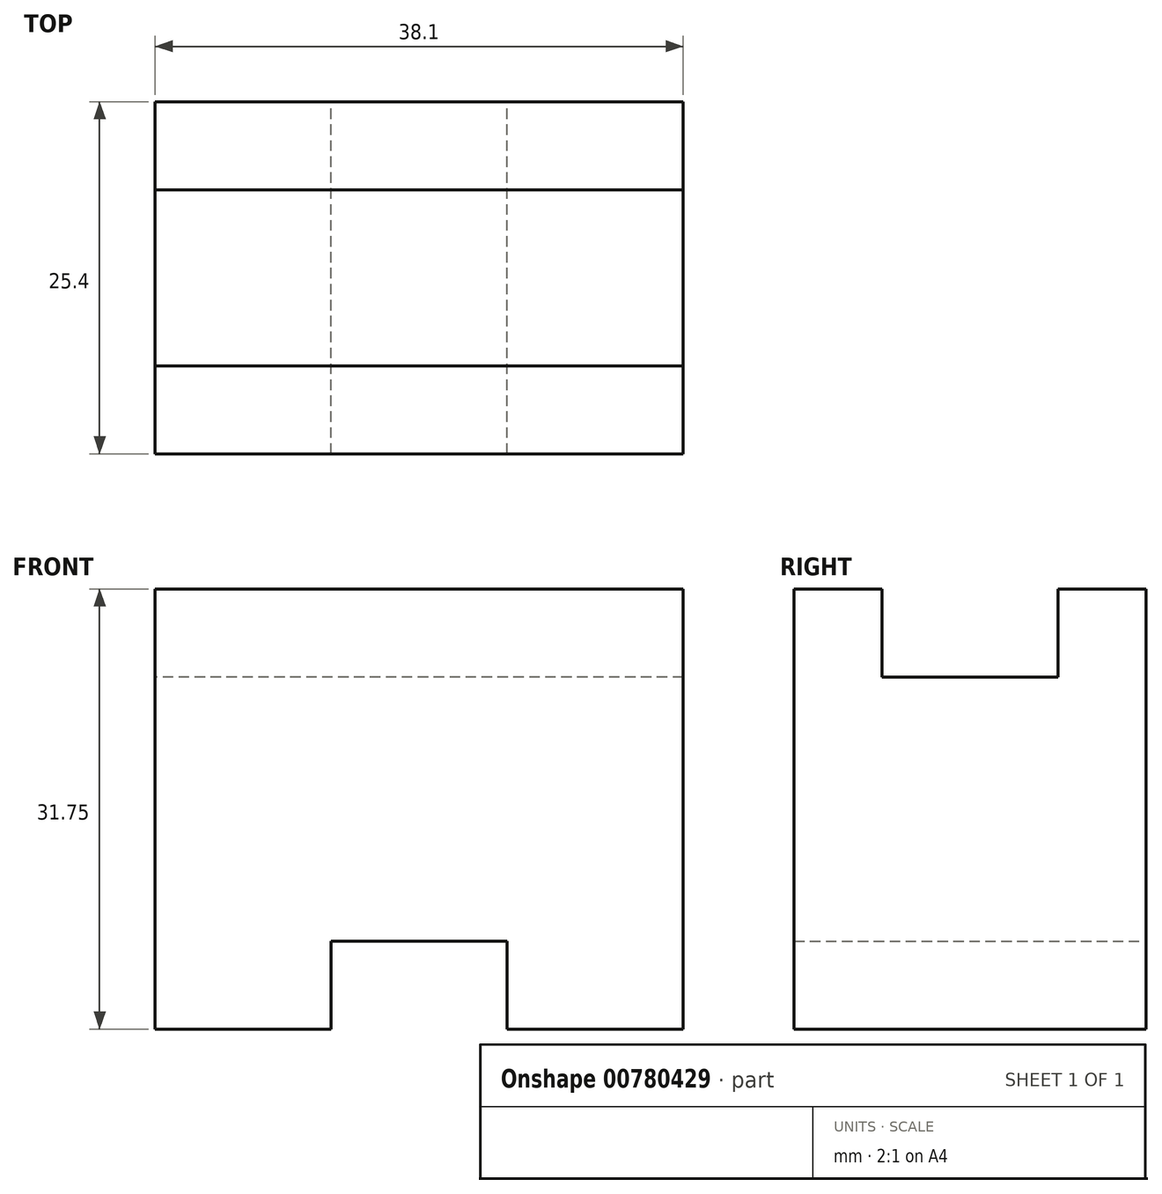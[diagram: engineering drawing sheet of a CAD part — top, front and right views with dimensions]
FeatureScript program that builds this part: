
annotation { "Feature Type Name" : "Feature", "Feature Type Description" : "" }
export const myFeature = defineFeature(function(context is Context, id is Id, definition is map)
    precondition{}
    {
        {
            var Q0;
            Q0=qCreatedBy(makeId("Front.planeOp"),FACE);
            var sketch = newSketch(context, id + "F0", { "sketchPlane" : qUnion([Q0])});
            skLineSegment(sketch, "E0", {"start": v(0, 0) * mm, "end": v(-12.7, 0) * mm});
            skLineSegment(sketch, "E1", {"start": v(-12.7, 0) * mm, "end": v(-12.7, 6.35) * mm});
            skLineSegment(sketch, "E2", {"start": v(-12.7, 6.35) * mm, "end": v(-25.4, 6.35) * mm});
            skLineSegment(sketch, "E3", {"start": v(-25.4, 6.35) * mm, "end": v(-25.4, 0) * mm});
            skLineSegment(sketch, "E4", {"start": v(-25.4, 0) * mm, "end": v(-38.1, 0) * mm});
            skLineSegment(sketch, "E5", {"start": v(-38.1, 0) * mm, "end": v(-38.1, 31.75) * mm});
            skLineSegment(sketch, "E6", {"start": v(-38.1, 31.75) * mm, "end": v(0, 31.75) * mm});
            skLineSegment(sketch, "E7", {"start": v(0, 31.75) * mm, "end": v(0, 0) * mm});
            skSolve(sketch);
        }
        {
            var Q0;
            Q0=makeQuery(id+"F0.imprint","IMPRINT",FACE,{"disambiguationData":[TD([[makeQuery(id+"F0.imprint","IMPRINT",EDGE,{"derivedFrom":sQuery(id+"F0.wireOp",EDGE,"E0")}),-1.0]])]});
            extrude(context, id + "F1", {"entities" : qUnion([Q0]), "depth" : 25.4 * mm, "offsetDistance" : 25.4 * mm});
        }
        {
            var Q0;
            Q0=makeQuery(id+"F1.opExtrude","SWEPT_FACE",FACE,{"disambiguationData":[OSD([sQuery(id+"F0.wireOp",EDGE,"E6")])]});
            var sketch = newSketch(context, id + "F2", { "sketchPlane" : qUnion([Q0])});
            skLineSegment(sketch, "E8", {"start": v(0, 0) * mm, "end": v(0, -6.35) * mm});
            skLineSegment(sketch, "E9", {"start": v(0, -6.35) * mm, "end": v(-38.1, -6.35) * mm});
            skLineSegment(sketch, "E10", {"start": v(-38.1, -6.35) * mm, "end": v(-38.1, -19.05) * mm});
            skLineSegment(sketch, "E11", {"start": v(-38.1, -19.05) * mm, "end": v(0, -19.05) * mm});
            skLineSegment(sketch, "E12", {"start": v(0, -19.05) * mm, "end": v(0, -6.35) * mm});
            skSolve(sketch);
        }
        {
            var Q0;
            Q0=makeQuery(id+"F2.imprint","IMPRINT",FACE,{"disambiguationData":[TD([[makeQuery(id+"F2.imprint","IMPRINT",EDGE,{"derivedFrom":sQuery(id+"F2.wireOp",EDGE,"E9")}),1.0]])]});
            extrude(context, id + "F3", {"entities" : qUnion([Q0]), "operationType" : NewBodyOperationType.REMOVE, "oppositeDirection" : true, "depth" : 6.35 * mm, "offsetDistance" : 25.4 * mm});
        }
    });
